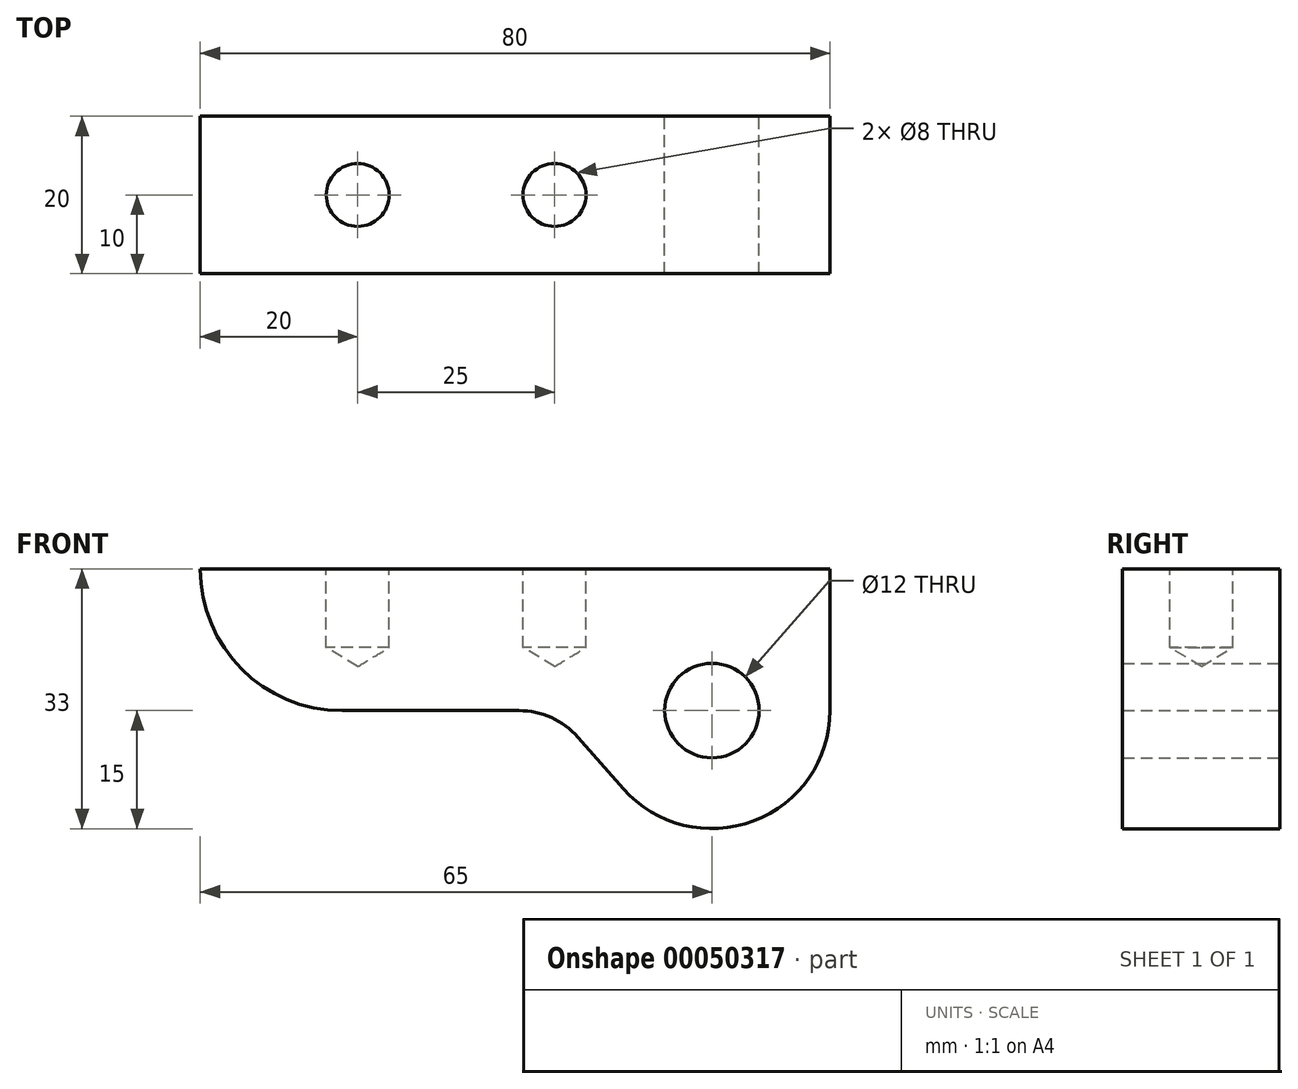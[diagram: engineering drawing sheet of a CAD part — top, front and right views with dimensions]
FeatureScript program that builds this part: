
annotation { "Feature Type Name" : "Feature", "Feature Type Description" : "" }
export const myFeature = defineFeature(function(context is Context, id is Id, definition is map)
    precondition{}
    {
        {
            var Q0;
            Q0=qCreatedBy(makeId("Front.planeOp"),FACE);
            var sketch = newSketch(context, id + "F0", { "sketchPlane" : qUnion([Q0])});
            skArc(sketch, "E0", {"start": v(-11.25, -9.92) * mm, "mid": v(5.3, -14.03) * mm, "end": v(15, 0) * mm});
            skCircle(sketch, "E1", {"center": v(0, 0) * mm, "radius": 6 * mm});
            skLineSegment(sketch, "E2", {"start": v(15, 0) * mm, "end": v(15, 15) * mm});
            skLineSegment(sketch, "E3", {"start": v(0, 15) * mm, "end": v(15, 15) * mm, "construction": true});
            skLineSegment(sketch, "E4", {"start": v(-20, 0) * mm, "end": v(-11.25, -9.92) * mm});
            skLineSegment(sketch, "E5", {"start": v(15, 15) * mm, "end": v(15, 18) * mm});
            skLineSegment(sketch, "E6", {"start": v(15, 18) * mm, "end": v(-65, 18) * mm});
            skLineSegment(sketch, "E7", {"start": v(-65, 18) * mm, "end": v(-65, 18) * mm});
            skLineSegment(sketch, "E8", {"start": v(-65, 18) * mm, "end": v(-65, 0) * mm});
            skLineSegment(sketch, "E9", {"start": v(-20, 0) * mm, "end": v(-65, 0) * mm});
            skSolve(sketch);
        }
        {
            var Q0;
            Q0 = qSketchRegion(id + "F0", true);
            extrude(context, id + "F1", {"entities" : qUnion([Q0]), "depth" : 20 * mm});
        }
        {
            var Q0;
            Q0=makeQuery(id+"F1.opExtrude","SWEPT_EDGE",EDGE,{"disambiguationData":[OSD([sQuery(id+"F0.wireOp",EDGE,"a2aba057-fbfd-402d-8635-e12b28344d63"),sQuery(id+"F0.wireOp",EDGE,"E4")])]});
            fillet(context, id + "F2", {"entities" : qUnion([Q0]), "radius" : 10 * mm, "tangentPropagation" : true, "allowEdgeOverflow" : false});
        }
        {
            var Q0;
            Q0=makeQuery(id+"F1.opExtrude","SWEPT_FACE",FACE,{"disambiguationData":[OSD([sQuery(id+"F0.wireOp",EDGE,"E6")])]});
            var sketch = newSketch(context, id + "F3", { "sketchPlane" : qUnion([Q0])});
            skPoint(sketch, "E10", {"position": v(-45, -10) * mm});
            skLineSegment(sketch, "E11", {"start": v(-47.23, -10) * mm, "end": v(14.28, -10) * mm, "construction": true});
            skPoint(sketch, "E12", {"position": v(-20, -10) * mm});
            skSolve(sketch);
        }
        {
            var Q0;
            Q0=sQuery(id+"F3.wireOp",VERTEX,"E10");
            var Q1;
            Q1=sQuery(id+"F3.wireOp",VERTEX,"E12");
            var Q2;
            Q2=makeQuery(id+"F1.opExtrude","SWEPT_BODY",BODY,{"disambiguationData":[OSD([sQuery(id+"F0.wireOp",EDGE,"E0"),sQuery(id+"F0.wireOp",EDGE,"E1"),sQuery(id+"F0.wireOp",EDGE,"E2"),sQuery(id+"F0.wireOp",EDGE,"E3"),sQuery(id+"F0.wireOp",EDGE,"5b80f325-95c3-4fa4-8af3-c565095338d7"),sQuery(id+"F0.wireOp",EDGE,"47618bab-31b4-4032-abc7-7421dac63343"),sQuery(id+"F0.wireOp",EDGE,"5dfdea00-026b-412a-862d-19720f05f2e6"),sQuery(id+"F0.wireOp",EDGE,"a2aba057-fbfd-402d-8635-e12b28344d63"),sQuery(id+"F0.wireOp",EDGE,"E4")])]});
            hole(context, id + "F4", {"style" : HoleStyle.SIMPLE, "holeDiameter" : 8 * mm, "endStyle" : HoleEndStyle.BLIND, "holeDepth" : 10 * mm, "locations" : qUnion([Q0, Q1]), "scope" : qUnion([Q2])});
        }
        {
            var Q0;
            Q0=makeQuery(id+"F1.opExtrude","SWEPT_EDGE",EDGE,{"disambiguationData":[OSD([sQuery(id+"F0.wireOp",EDGE,"E8"),sQuery(id+"F0.wireOp",EDGE,"E9")])]});
            fillet(context, id + "F5", {"entities" : qUnion([Q0]), "radius" : 18 * mm, "tangentPropagation" : true, "allowEdgeOverflow" : false});
        }
    });
